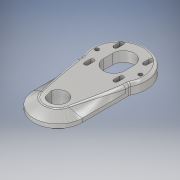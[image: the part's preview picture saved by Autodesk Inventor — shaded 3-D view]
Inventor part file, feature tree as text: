
AUTODESK INVENTOR PART (.ipt)
format: ipt  version: 2019.2 (Build 232265000, 265)  size: 330,752 bytes
history: native  units: mm
features: extrude x6, sketch x5, fillet x2, thread x2, plane x1, loft x1
ambient origin geometry x8: Origin, YZ Plane, XZ Plane, XY Plane, X Axis, Y Axis, Z Axis, Center Point
bodies: Solid1 (feature_tree)
feature tree (17):
  sketch  "Sketch1"  dims[d1=57.0mm d2=25.0mm]
  plane  "Work Plane1"
  sketch  "Sketch2"  dims[d3=19.0mm d4=116.5mm]
  loft  "Loft1"
  extrude  "Extrusion1"  Depth=116.5mm
  extrude  "Extrusion2"  Depth=52.0mm
  extrude  "Extrusion3"  Depth=45.0mm
  fillet  "Fillet1"  Radius=4.0mm
  thread  "Thread1"  [1 undecoded]
  thread  "Thread2"  [1 undecoded]
  extrude  "Extrusion6"  TaperAngle=0.0deg  [1 undecoded]
  fillet  "Fillet4"  [1 undecoded]
  extrude  "Extrusion7"  Depth=10.0mm TaperAngle=0.0deg
  extrude  "Extrusion9"  Depth=10.0mm TaperAngle=0.0deg
  sketch  "Sketch7"  dims[d8=43.117mm d9=45.0mm d10=4.0mm d16=4.0mm d17=6.5mm]
  sketch  "Sketch8"  dims[d18=4.0mm d19=0.0mm d20=0.0mm d21=90.0deg d22=0.0mm d23=90.0deg d24=5.0mm d25=0.0mm d27=10.0mm d28=0.0mm d29=3.0mm d72=10.0mm d73=0.0mm d74=10.0mm d75=0.0mm d76=2.0mm d77=10.0mm d78=0.0mm d79=2.0mm d80=3.0mm d81=4.2mm d82=3.0mm d83=90.0deg d84=4.2mm d85=3.0mm d86=90.0deg d87=4.2mm d88=3.0mm d89=90.0deg d90=4.2mm d91=10.0mm d92=0.0mm d94=22.0mm d100=2.443461mm d101=1.2mm d102=10.0mm d103=0.0mm]
  sketch  "Sketch6"  dims[d5=63.0mm d6=52.0mm]
note: 4 required parameter values undecoded (feature->parameter linkage not recoverable at this tier; creation-order binding heuristic only, values carry confidence <= 0.55)
